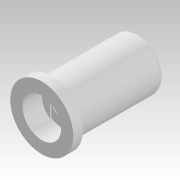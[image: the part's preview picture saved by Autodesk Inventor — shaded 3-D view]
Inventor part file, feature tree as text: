
AUTODESK INVENTOR PART (.ipt)
format: ipt  version: 2020 (Build 240168000, 168)  size: 137,216 bytes
history: native  units: mm
features: sketch x2, revolve x1, fillet x1, extrude x1
ambient origin geometry x8: Origin, YZ Plane, XZ Plane, XY Plane, X Axis, Y Axis, Z Axis, Center Point
bodies: Solid1 (feature_tree)
feature tree (5):
  revolve  "Revolution1"  [1 undecoded]
  fillet  "Fillet1"  Radius=1.0mm
  extrude  "Extrusion1"  Depth=13.5mm
  sketch  "Sketch1"  dims[d0=1.7mm d1=3.9mm d2=1.0mm]
  sketch  "Sketch2"  dims[d3=1.5mm d4=13.5mm d5=90.0deg d6=3.0mm d7=3.0mm d8=0.5mm d9=0.2mm d10=0.0mm]
note: 1 required parameter value undecoded (feature->parameter linkage not recoverable at this tier; creation-order binding heuristic only, values carry confidence <= 0.55)
